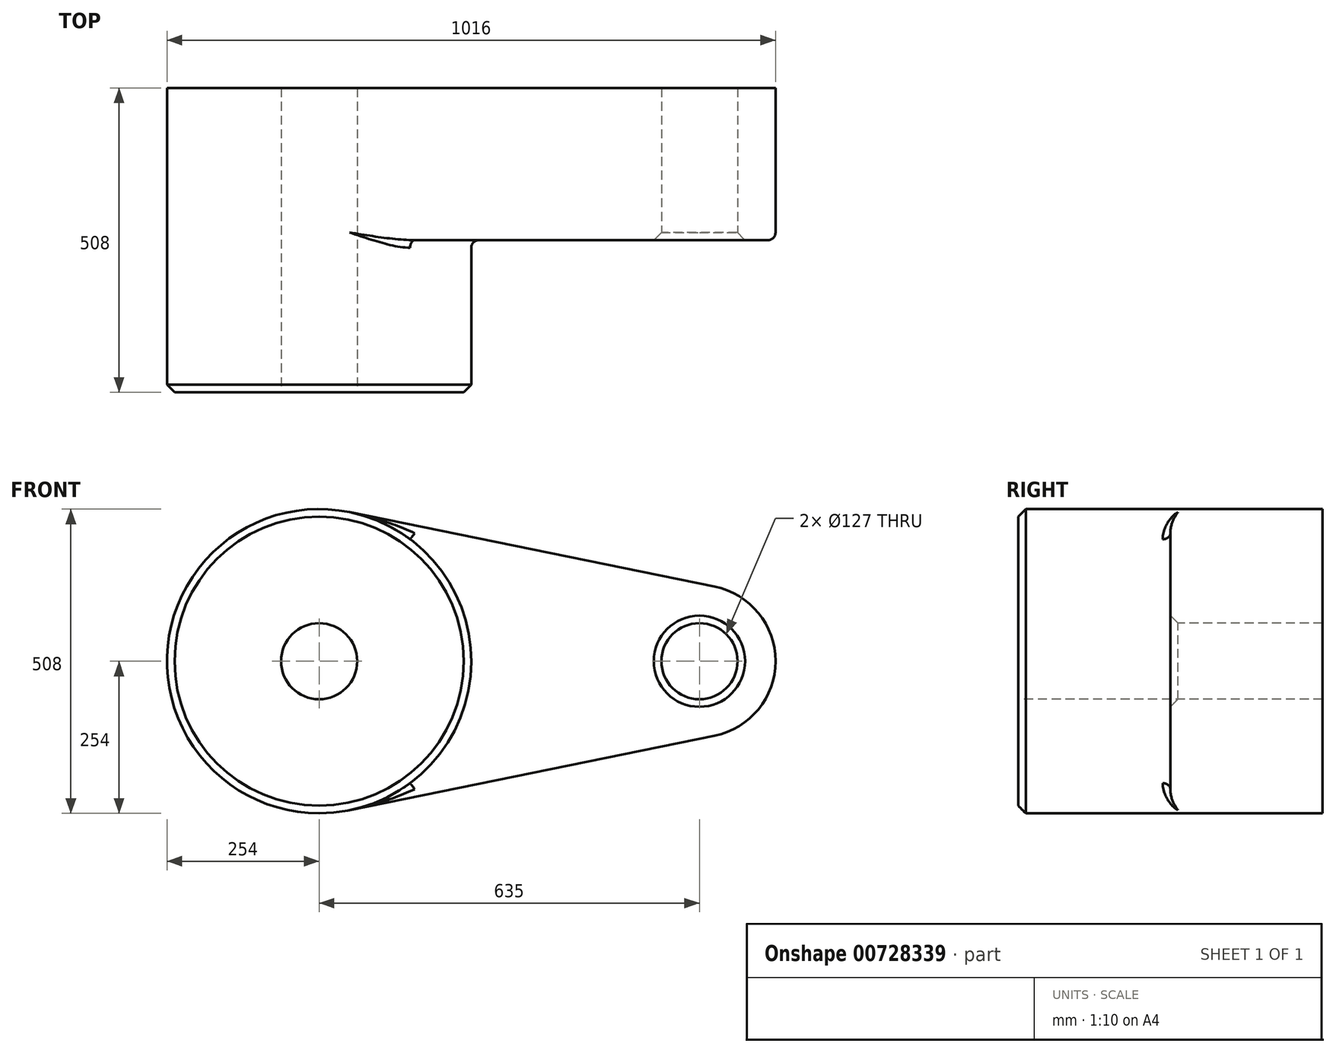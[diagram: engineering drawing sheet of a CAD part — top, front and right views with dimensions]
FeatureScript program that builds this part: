
annotation { "Feature Type Name" : "Feature", "Feature Type Description" : "" }
export const myFeature = defineFeature(function(context is Context, id is Id, definition is map)
    precondition{}
    {
        {
            var Q0;
            Q0=qCreatedBy(makeId("Front.planeOp"),FACE);
            var sketch = newSketch(context, id + "F0", { "sketchPlane" : qUnion([Q0])});
            skCircle(sketch, "E0", {"center": v(0, 0) * mm, "radius": 254 * mm});
            skCircle(sketch, "E1", {"center": v(635, 0) * mm, "radius": 127 * mm});
            skLineSegment(sketch, "E2", {"start": v(50.8, 248.87) * mm, "end": v(660.4, 124.43) * mm});
            skLineSegment(sketch, "E3", {"start": v(50.8, -248.87) * mm, "end": v(660.4, -124.43) * mm});
            skSolve(sketch);
        }
        {
            var Q0;
            {var subQ0=sQuery(id+"F0.wireOp",EDGE,"E2");Q0=makeQuery(id+"F0.imprint","IMPRINT",FACE,{"disambiguationData":[TD([[makeQuery(id+"F0.imprint","IMPRINT",EDGE,{"derivedFrom":subQ0}),-1.0]])]});}
            var Q1;
            {var subQ0=sQuery(id+"F0.wireOp",EDGE,"E0");var subQ1=makeQuery(id+"F0.imprint","INTERSECT",VERTEX,{"derivedFrom":[subQ0,sQuery(id+"F0.wireOp",EDGE,"E2")]});Q1=makeQuery(id+"F0.imprint","IMPRINT",FACE,{"disambiguationData":[TD([[makeQuery(id+"F0.imprint","IMPRINT",EDGE,{"disambiguationData":[TD([[subQ1,-1.0]])],"derivedFrom":subQ0}),1.0]])]});}
            var Q2;
            {var subQ0=sQuery(id+"F0.wireOp",EDGE,"E1");var subQ1=makeQuery(id+"F0.imprint","INTERSECT",VERTEX,{"derivedFrom":[subQ0,sQuery(id+"F0.wireOp",EDGE,"E2")]});Q2=makeQuery(id+"F0.imprint","IMPRINT",FACE,{"disambiguationData":[TD([[makeQuery(id+"F0.imprint","IMPRINT",EDGE,{"disambiguationData":[TD([[subQ1,-1.0]])],"derivedFrom":subQ0}),1.0]])]});}
            extrude(context, id + "F1", {"entities" : qUnion([Q0, Q1, Q2]), "depth" : 254 * mm, "offsetDistance" : 25.4 * mm});
        }
        {
            var Q0;
            {var subQ0=sQuery(id+"F0.wireOp",EDGE,"E0");var subQ1=makeQuery(id+"F0.imprint","INTERSECT",VERTEX,{"derivedFrom":[subQ0,sQuery(id+"F0.wireOp",EDGE,"E2")]});Q0=makeQuery(id+"F0.imprint","IMPRINT",FACE,{"disambiguationData":[TD([[makeQuery(id+"F0.imprint","IMPRINT",EDGE,{"disambiguationData":[TD([[subQ1,-1.0]])],"derivedFrom":subQ0}),1.0]])]});}
            extrude(context, id + "F2", {"entities" : qUnion([Q0]), "operationType" : NewBodyOperationType.ADD, "depth" : 508 * mm, "offsetDistance" : 25.4 * mm});
        }
        {
            var Q0;
            Q0=makeQuery(id+"F2.opExtrude","CAP_FACE",FACE,{"disambiguationData":[OSD([sQuery(id+"F0.wireOp",EDGE,"E0")])],"isStart":false});
            var sketch = newSketch(context, id + "F3", { "sketchPlane" : qUnion([Q0])});
            skCircle(sketch, "E4", {"center": v(0, 0) * mm, "radius": 63.5 * mm});
            skCircle(sketch, "E5", {"center": v(635, 0) * mm, "radius": 63.5 * mm});
            skSolve(sketch);
        }
        {
            var Q0;
            Q0 = qSketchRegion(id + "F3", true);
            extrude(context, id + "F4", {"entities" : qUnion([Q0]), "operationType" : NewBodyOperationType.REMOVE, "oppositeDirection" : true, "depth" : 635 * mm, "offsetDistance" : 25.4 * mm});
        }
        {
            var Q0;
            Q0=makeQuery(id+"F4.boolean.opBoolean","COPY",EDGE,{"derivedFrom":makeQuery(id+"F4.opExtrude","CAP_EDGE",EDGE,{"disambiguationData":[OSD([sQuery(id+"F3.wireOp",EDGE,"E4")])],"isStart":true})});
            var Q1;
            Q1=makeQuery(id+"F4.boolean.opBoolean","INTERSECT",EDGE,{"derivedFrom":[makeQuery(id+"F1.opExtrude","CAP_FACE",FACE,{"disambiguationData":[OSD([sQuery(id+"F0.wireOp",EDGE,"E0"),sQuery(id+"F0.wireOp",EDGE,"E1"),sQuery(id+"F0.wireOp",EDGE,"E2"),sQuery(id+"F0.wireOp",EDGE,"E3")])],"isStart":false}),makeQuery(id+"F4.opExtrude","SWEPT_FACE",FACE,{"disambiguationData":[OSD([sQuery(id+"F3.wireOp",EDGE,"E5")])]})]});
            var Q2;
            Q2=makeQuery(id+"F2.opExtrude","CAP_EDGE",EDGE,{"disambiguationData":[OSD([sQuery(id+"F0.wireOp",EDGE,"E0")])],"isStart":false});
            chamfer(context, id + "F5", {"entities" : qUnion([Q0, Q1, Q2]), "width" : 12.7 * mm, "tangentPropagation" : true});
        }
        {
            var Q0;
            Q0=makeQuery(id+"F1.opExtrude","CAP_EDGE",EDGE,{"disambiguationData":[OSD([sQuery(id+"F0.wireOp",EDGE,"E2")])],"isStart":false});
            var Q1;
            Q1=makeQuery(id+"F1.opExtrude","CAP_EDGE",EDGE,{"disambiguationData":[OSD([sQuery(id+"F0.wireOp",EDGE,"E1")])],"isStart":false});
            var Q2;
            Q2=makeQuery(id+"F1.opExtrude","CAP_EDGE",EDGE,{"disambiguationData":[OSD([sQuery(id+"F0.wireOp",EDGE,"E3")])],"isStart":false});
            var Q3;
            {var subQ0=sQuery(id+"F0.wireOp",EDGE,"E0");Q3=makeQuery(id+"F2.boolean.opBoolean","INTERSECT",EDGE,{"derivedFrom":[makeQuery(id+"F1.opExtrude","CAP_FACE",FACE,{"disambiguationData":[OSD([subQ0,sQuery(id+"F0.wireOp",EDGE,"E1"),sQuery(id+"F0.wireOp",EDGE,"E2"),sQuery(id+"F0.wireOp",EDGE,"E3")])],"isStart":false}),makeQuery(id+"F2.opExtrude","SWEPT_FACE",FACE,{"disambiguationData":[OSD([subQ0])]})]});}
            fillet(context, id + "F6", {"entities" : qUnion([Q0, Q1, Q2, Q3]), "radius" : 12.7 * mm, "tangentPropagation" : true, "allowEdgeOverflow" : false});
        }
    });
